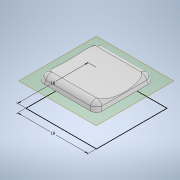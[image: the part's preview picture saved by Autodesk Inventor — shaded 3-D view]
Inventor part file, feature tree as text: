
AUTODESK INVENTOR PART (.ipt)
format: ipt  version: 2022 (Build 260153000, 153)  size: 196,096 bytes
history: native  units: in
note: dims shown in document units (in); Inventor stores cm internally (conversion verified against a paired STEP export)
features: extrude x6, sketch x6, plane x2, fillet x1, split x1
ambient origin geometry x8: Origin, YZ Plane, XZ Plane, XY Plane, X Axis, Y Axis, Z Axis, Center Point
bodies: Solid1 (feature_tree)
feature tree (16):
  extrude  "Extrusion1"  Depth=0.7087in
  fillet  "Fillet1"  Radius=0.315in
  plane  "Work Plane1"
  extrude  "Extrusion2"  Depth=0.7087in
  extrude  "Extrusion3"  Depth=0.6299in
  extrude  "Extrusion4"  Depth=0.1772in
  extrude  "Extrusion5"  Depth=0.1575in TaperAngle=0.0deg
  plane  "Work Plane3"
  split  "Split1"
  extrude  "Extrusion7"  Depth=0.3937in
  sketch  "Sketch1"  dims[d0=0.7087in d1=0.7087in d2=0.315in d3=-0.1031in]
  sketch  "Sketch2"  dims[d4=0.0591in d5=0.7087in]
  sketch  "Sketch3"  dims[d6=0.0in d7=0.0in d8=0.6299in]
  sketch  "Sketch4"  dims[d9=0.6299in d10=0.1772in d11=-0.1031in]
  sketch  "Sketch5"  dims[d12=0.2185in d13=0.1575in d14=0.0in]
  sketch  "Sketch7"  dims[d15=0.0472in d16=0.1634in d17=0.1634in d18=0.0472in d19=0.0118in d20=0.1575in d21=0.0in d24=-0.2362in d25=0.3937in d26=0.0in]
